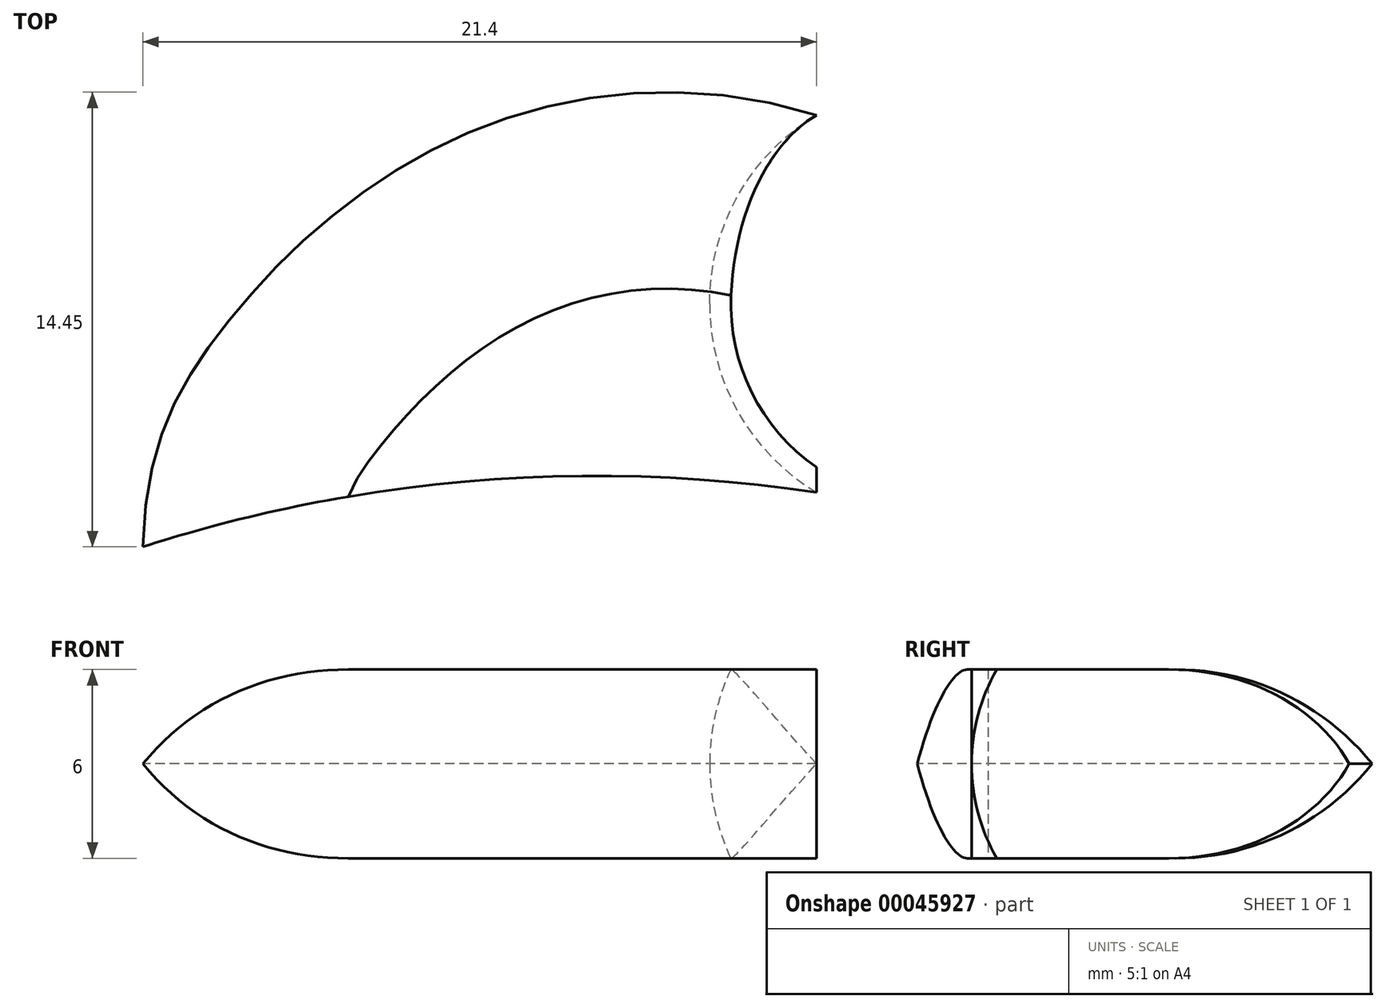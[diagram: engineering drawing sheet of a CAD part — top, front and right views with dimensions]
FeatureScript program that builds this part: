
annotation { "Feature Type Name" : "Feature", "Feature Type Description" : "" }
export const myFeature = defineFeature(function(context is Context, id is Id, definition is map)
    precondition{}
    {
        {
            var Q0;
            Q0=qCreatedBy(makeId("Top.planeOp"),FACE);
            var sketch = newSketch(context, id + "F0", { "sketchPlane" : qUnion([Q0])});
            skFitSpline(sketch, "E0", {"points": [v(0, 14.12) * mm, v(-11.78, 13.23) * mm, v(-18.73, 7.5) * mm, v(-21.4, 0.4) * mm], "startDerivative": vector(-34.32, 10.64) * mm, "endDerivative": vector(-0.59, -32.15) * mm});
            skArc(sketch, "E1", {"start": v(0, 2.12) * mm, "mid": v(-10.8, 2.5) * mm, "end": v(-21.4, 0.4) * mm});
            skLineSegment(sketch, "E2", {"start": v(0, 14.12) * mm, "end": v(0, 2.12) * mm});
            skSolve(sketch);
        }
        {
            var Q0;
            Q0=makeQuery(id+"F0.imprint","IMPRINT",FACE,{"disambiguationData":[TD([[makeQuery(id+"F0.imprint","IMPRINT",EDGE,{"derivedFrom":sQuery(id+"F0.wireOp",EDGE,"E0")}),1.0]])]});
            extrude(context, id + "F1", {"entities" : qUnion([Q0]), "depth" : 3 * mm});
        }
        {
            var Q0;
            Q0=makeQuery(id+"F1.opExtrude","CAP_EDGE",EDGE,{"disambiguationData":[OSD([sQuery(id+"F0.wireOp",EDGE,"E0")])],"isStart":false});
            fillet(context, id + "F2", {"entities" : qUnion([Q0]), "radius" : 8 * mm, "tangentPropagation" : true, "allowEdgeOverflow" : false});
        }
        {
            var Q0;
            Q0=makeQuery(id+"F1.opExtrude","SWEPT_BODY",BODY,{"disambiguationData":[OSD([sQuery(id+"F0.wireOp",EDGE,"E0"),sQuery(id+"F0.wireOp",EDGE,"E1"),sQuery(id+"F0.wireOp",EDGE,"51b7d86f-bf91-46a9-8d24-dce520e18d72")])]});
            var Q1;
            Q1=qCreatedBy(makeId("Top.planeOp"),FACE);
            mirror(context, id + "F3", {"operationType" : NewBodyOperationType.ADD, "entities" : qUnion([Q0]), "mirrorPlane" : qUnion([Q1])});
        }
        {
            var Q0;
            Q0=qCreatedBy(makeId("Top.planeOp"),FACE);
            var sketch = newSketch(context, id + "F4", { "sketchPlane" : qUnion([Q0])});
            skArc(sketch, "E3", {"start": v(0, 14.12) * mm, "mid": v(-3.4, 8.12) * mm, "end": v(0, 2.12) * mm});
            skLineSegment(sketch, "E4", {"start": v(0, 14.12) * mm, "end": v(0, 2.12) * mm});
            skLineSegment(sketch, "E5", {"start": v(0, 8.12) * mm, "end": v(-3.4, 8.12) * mm});
            skSolve(sketch);
        }
        {
            var Q0;
            {var subQ3=sQuery(id+"F4.wireOp",EDGE,"E5");Q0=makeQuery(id+"F4.imprint","IMPRINT",FACE,{"disambiguationData":[TD([[makeQuery(id+"F4.imprint","IMPRINT",EDGE,{"derivedFrom":subQ3}),-1.0]])]});}
            var Q1;
            Q1=sQuery(id+"F4.wireOp",EDGE,"E5");
            revolve(context, id + "F5", {"operationType" : NewBodyOperationType.REMOVE, "entities" : qUnion([Q0]), "axis" : qUnion([Q1]), "revolveType" : RevolveType.FULL});
        }
    });
